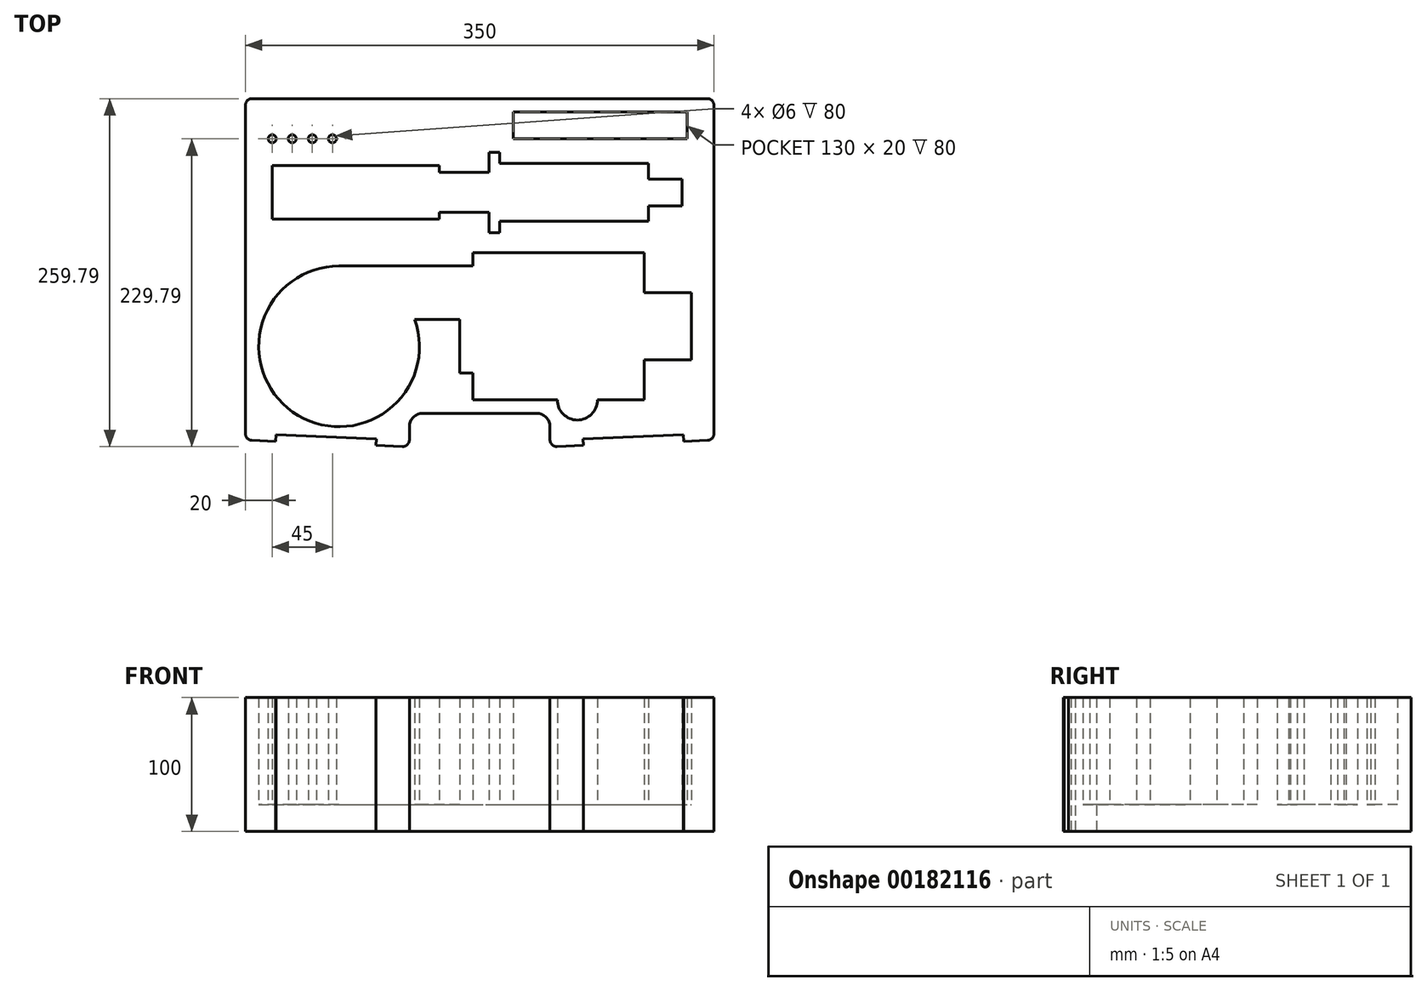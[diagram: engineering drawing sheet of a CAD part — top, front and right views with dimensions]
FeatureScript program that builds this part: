
annotation { "Feature Type Name" : "Feature", "Feature Type Description" : "" }
export const myFeature = defineFeature(function(context is Context, id is Id, definition is map)
    precondition{}
    {
        {
            var Q0;
            Q0=qCreatedBy(makeId("Top.planeOp"),FACE);
            var sketch = newSketch(context, id + "F0", { "sketchPlane" : qUnion([Q0])});
            skLineSegment(sketch, "E0.bottom", {"start": v(345, 0) * mm, "end": v(5, 0) * mm});
            skLineSegment(sketch, "E1.top", {"start": v(217.5, -235) * mm, "end": v(132.5, -235) * mm});
            skLineSegment(sketch, "E1.left", {"start": v(227.5, -254.8) * mm, "end": v(227.5, -245) * mm});
            skLineSegment(sketch, "E1.right", {"start": v(122.5, -254.8) * mm, "end": v(122.5, -245) * mm});
            skLineSegment(sketch, "E2", {"start": v(350, -5) * mm, "end": v(350, -250.2) * mm});
            skLineSegment(sketch, "E3", {"start": v(0, -5) * mm, "end": v(0, -250.2) * mm});
            skLineSegment(sketch, "E4", {"start": v(327.42, -255.92) * mm, "end": v(327.21, -250.93) * mm});
            skLineSegment(sketch, "E5", {"start": v(327.21, -250.93) * mm, "end": v(252.28, -253.98) * mm});
            skLineSegment(sketch, "E6", {"start": v(252.28, -253.98) * mm, "end": v(252.48, -258.98) * mm});
            skLineSegment(sketch, "E7", {"start": v(97.52, -258.98) * mm, "end": v(97.72, -253.98) * mm});
            skLineSegment(sketch, "E8", {"start": v(97.72, -253.98) * mm, "end": v(22.79, -250.93) * mm});
            skLineSegment(sketch, "E9", {"start": v(22.79, -250.93) * mm, "end": v(22.58, -255.92) * mm});
            skLineSegment(sketch, "E10", {"start": v(22.58, -255.92) * mm, "end": v(4.8, -255.2) * mm});
            skLineSegment(sketch, "E11", {"start": v(97.52, -258.98) * mm, "end": v(117.3, -259.79) * mm});
            skLineSegment(sketch, "E12", {"start": v(252.48, -258.98) * mm, "end": v(232.7, -259.79) * mm});
            skLineSegment(sketch, "E13", {"start": v(345.2, -255.2) * mm, "end": v(327.42, -255.92) * mm});
            skPoint(sketch, "E14.visualSharp", {"position": v(227.5, -235) * mm});
            skArc(sketch, "E14.filletArc", {"start": v(227.5, -245) * mm, "mid": v(224.57, -237.93) * mm, "end": v(217.5, -235) * mm});
            skPoint(sketch, "E15.visualSharp", {"position": v(122.5, -235) * mm});
            skArc(sketch, "E15.filletArc", {"start": v(132.5, -235) * mm, "mid": v(125.43, -237.93) * mm, "end": v(122.5, -245) * mm});
            skPoint(sketch, "E16.visualSharp", {"position": v(0, -255) * mm});
            skArc(sketch, "E16.filletArc", {"start": v(0, -250.2) * mm, "mid": v(1.4, -253.66) * mm, "end": v(4.8, -255.2) * mm});
            skPoint(sketch, "E17.visualSharp", {"position": v(350, -255) * mm});
            skArc(sketch, "E17.filletArc", {"start": v(345.2, -255.2) * mm, "mid": v(348.6, -253.66) * mm, "end": v(350, -250.2) * mm});
            skPoint(sketch, "E18.visualSharp", {"position": v(350, 0) * mm});
            skArc(sketch, "E18.filletArc", {"start": v(350, -5) * mm, "mid": v(348.54, -1.46) * mm, "end": v(345, 0) * mm});
            skPoint(sketch, "E19.visualSharp", {"position": v(0, 0) * mm});
            skArc(sketch, "E19.filletArc", {"start": v(5, 0) * mm, "mid": v(1.46, -1.46) * mm, "end": v(0, -5) * mm});
            skPoint(sketch, "E20.visualSharp", {"position": v(227.5, -260) * mm});
            skArc(sketch, "E20.filletArc", {"start": v(227.5, -254.8) * mm, "mid": v(229.04, -258.4) * mm, "end": v(232.7, -259.79) * mm});
            skPoint(sketch, "E21.visualSharp", {"position": v(122.5, -260) * mm});
            skArc(sketch, "E21.filletArc", {"start": v(117.3, -259.79) * mm, "mid": v(120.96, -258.4) * mm, "end": v(122.5, -254.8) * mm});
            skLineSegment(sketch, "E22.bottom", {"start": v(20, -50) * mm, "end": v(145, -50) * mm});
            skLineSegment(sketch, "E22.top", {"start": v(20, -90) * mm, "end": v(145, -90) * mm});
            skLineSegment(sketch, "E22.left", {"start": v(20, -50) * mm, "end": v(20, -90) * mm});
            skLineSegment(sketch, "E23", {"start": v(20, -70) * mm, "end": v(326, -70) * mm, "construction": true});
            skLineSegment(sketch, "E24.bottom", {"start": v(182, -40) * mm, "end": v(190, -40) * mm});
            skLineSegment(sketch, "E24.top", {"start": v(182, -100) * mm, "end": v(190, -100) * mm});
            skLineSegment(sketch, "E25.bottom", {"start": v(145, -55) * mm, "end": v(182, -55) * mm});
            skLineSegment(sketch, "E25.top", {"start": v(145, -85) * mm, "end": v(182, -85) * mm});
            skLineSegment(sketch, "E26.bottom", {"start": v(190, -48.5) * mm, "end": v(301, -48.5) * mm});
            skLineSegment(sketch, "E26.top", {"start": v(190, -91.5) * mm, "end": v(301, -91.5) * mm});
            skLineSegment(sketch, "E27.bottom", {"start": v(301, -60) * mm, "end": v(326, -60) * mm});
            skLineSegment(sketch, "E27.top", {"start": v(301, -80) * mm, "end": v(326, -80) * mm});
            skLineSegment(sketch, "E27.right", {"start": v(326, -60) * mm, "end": v(326, -80) * mm});
            skLineSegment(sketch, "E28", {"start": v(145, -50) * mm, "end": v(145, -55) * mm});
            skLineSegment(sketch, "E29", {"start": v(145, -90) * mm, "end": v(145, -85) * mm});
            skLineSegment(sketch, "E30", {"start": v(182, -85) * mm, "end": v(182, -100) * mm});
            skLineSegment(sketch, "E31", {"start": v(190, -100) * mm, "end": v(190, -91.5) * mm});
            skLineSegment(sketch, "E32", {"start": v(182, -55) * mm, "end": v(182, -40) * mm});
            skLineSegment(sketch, "E33", {"start": v(190, -40) * mm, "end": v(190, -48.5) * mm});
            skLineSegment(sketch, "E34", {"start": v(301, -48.5) * mm, "end": v(301, -60) * mm});
            skLineSegment(sketch, "E35", {"start": v(301, -80) * mm, "end": v(301, -91.5) * mm});
            skLineSegment(sketch, "E36.bottom", {"start": v(200, -10) * mm, "end": v(330, -10) * mm});
            skLineSegment(sketch, "E36.top", {"start": v(200, -30) * mm, "end": v(330, -30) * mm});
            skLineSegment(sketch, "E36.left", {"start": v(200, -10) * mm, "end": v(200, -30) * mm});
            skLineSegment(sketch, "E36.right", {"start": v(330, -10) * mm, "end": v(330, -30) * mm});
            skLineSegment(sketch, "E37", {"start": v(200, -20) * mm, "end": v(330, -20) * mm, "construction": true});
            skLineSegment(sketch, "E38.bottom", {"start": v(170, -115) * mm, "end": v(298, -115) * mm});
            skLineSegment(sketch, "E38.top", {"start": v(170, -225) * mm, "end": v(233, -225) * mm});
            skLineSegment(sketch, "E38.left", {"start": v(170, -115) * mm, "end": v(170, -125) * mm});
            skLineSegment(sketch, "E38.right", {"start": v(298, -115) * mm, "end": v(298, -145) * mm});
            skLineSegment(sketch, "E39.bottom", {"start": v(298, -145) * mm, "end": v(333, -145) * mm});
            skLineSegment(sketch, "E39.top", {"start": v(298, -195) * mm, "end": v(333, -195) * mm});
            skLineSegment(sketch, "E39.right", {"start": v(333, -145) * mm, "end": v(333, -195) * mm});
            skLineSegment(sketch, "E40.right", {"start": v(160, -165) * mm, "end": v(160, -205) * mm});
            skArc(sketch, "E41", {"start": v(70, -125) * mm, "mid": v(35.36, -233.99) * mm, "end": v(126.57, -165) * mm});
            skLineSegment(sketch, "E42", {"start": v(160, -165) * mm, "end": v(126.57, -165) * mm});
            skLineSegment(sketch, "E43.trimOffspring", {"start": v(170, -205) * mm, "end": v(170, -225) * mm});
            skLineSegment(sketch, "E44.trimOffspring", {"start": v(298, -195) * mm, "end": v(298, -225) * mm});
            skLineSegment(sketch, "E45", {"start": v(70, -125) * mm, "end": v(170, -125) * mm});
            skLineSegment(sketch, "E46", {"start": v(160, -205) * mm, "end": v(170, -205) * mm});
            skArc(sketch, "E47", {"start": v(233, -225) * mm, "mid": v(248, -240) * mm, "end": v(263, -225) * mm});
            skLineSegment(sketch, "E48.trimOffspring", {"start": v(263, -225) * mm, "end": v(298, -225) * mm});
            skCircle(sketch, "E49", {"center": v(20, -30) * mm, "radius": 3 * mm});
            skCircle(sketch, "E50.1.0.0", {"center": v(35, -30) * mm, "radius": 3 * mm});
            skCircle(sketch, "E50.2.0.0", {"center": v(50, -30) * mm, "radius": 3 * mm});
            skCircle(sketch, "E50.3.0.0", {"center": v(65, -30) * mm, "radius": 3 * mm});
            skLineSegment(sketch, "E50.direction1", {"start": v(20, -30) * mm, "end": v(35, -30) * mm, "construction": true});
            skSolve(sketch);
        }
        {
            var Q0;
            Q0=makeQuery(id+"F0.imprint","IMPRINT",FACE,{"disambiguationData":[TD([[makeQuery(id+"F0.imprint","IMPRINT",EDGE,{"derivedFrom":sQuery(id+"F0.wireOp",EDGE,"E0.bottom")}),1.0]])]});
            extrude(context, id + "F1", {"entities" : qUnion([Q0]), "depth" : 80 * mm});
        }
        {
            var Q0;
            Q0 = qSketchRegion(id + "F0", true);
            var Q1;
            Q1=makeQuery(id+"F0.imprint","IMPRINT",FACE,{"disambiguationData":[TD([[makeQuery(id+"F0.imprint","IMPRINT",EDGE,{"derivedFrom":sQuery(id+"F0.wireOp",EDGE,"E38.bottom")}),-1.0]])]});
            var Q2;
            Q2=makeQuery(id+"F0.imprint","IMPRINT",FACE,{"disambiguationData":[TD([[makeQuery(id+"F0.imprint","IMPRINT",EDGE,{"derivedFrom":sQuery(id+"F0.wireOp",EDGE,"E22.bottom")}),-1.0]])]});
            var Q3;
            Q3=makeQuery(id+"F0.imprint","IMPRINT",FACE,{"disambiguationData":[TD([[makeQuery(id+"F0.imprint","IMPRINT",EDGE,{"derivedFrom":sQuery(id+"F0.wireOp",EDGE,"E36.bottom")}),-1.0]])]});
            var Q4;
            Q4=makeQuery(id+"F0.imprint","IMPRINT",FACE,{"disambiguationData":[TD([[makeQuery(id+"F0.imprint","IMPRINT",EDGE,{"derivedFrom":sQuery(id+"F0.wireOp",EDGE,"E50.3.0.0")}),1.0]])]});
            var Q5;
            Q5=makeQuery(id+"F0.imprint","IMPRINT",FACE,{"disambiguationData":[TD([[makeQuery(id+"F0.imprint","IMPRINT",EDGE,{"derivedFrom":sQuery(id+"F0.wireOp",EDGE,"E50.2.0.0")}),1.0]])]});
            var Q6;
            Q6=makeQuery(id+"F0.imprint","IMPRINT",FACE,{"disambiguationData":[TD([[makeQuery(id+"F0.imprint","IMPRINT",EDGE,{"derivedFrom":sQuery(id+"F0.wireOp",EDGE,"E50.1.0.0")}),1.0]])]});
            var Q7;
            Q7=makeQuery(id+"F0.imprint","IMPRINT",FACE,{"disambiguationData":[TD([[makeQuery(id+"F0.imprint","IMPRINT",EDGE,{"derivedFrom":sQuery(id+"F0.wireOp",EDGE,"E49")}),1.0]])]});
            extrude(context, id + "F2", {"entities" : qUnion([Q0, Q1, Q2, Q3, Q4, Q5, Q6, Q7]), "operationType" : NewBodyOperationType.ADD, "oppositeDirection" : true, "depth" : 20 * mm});
        }
    });
